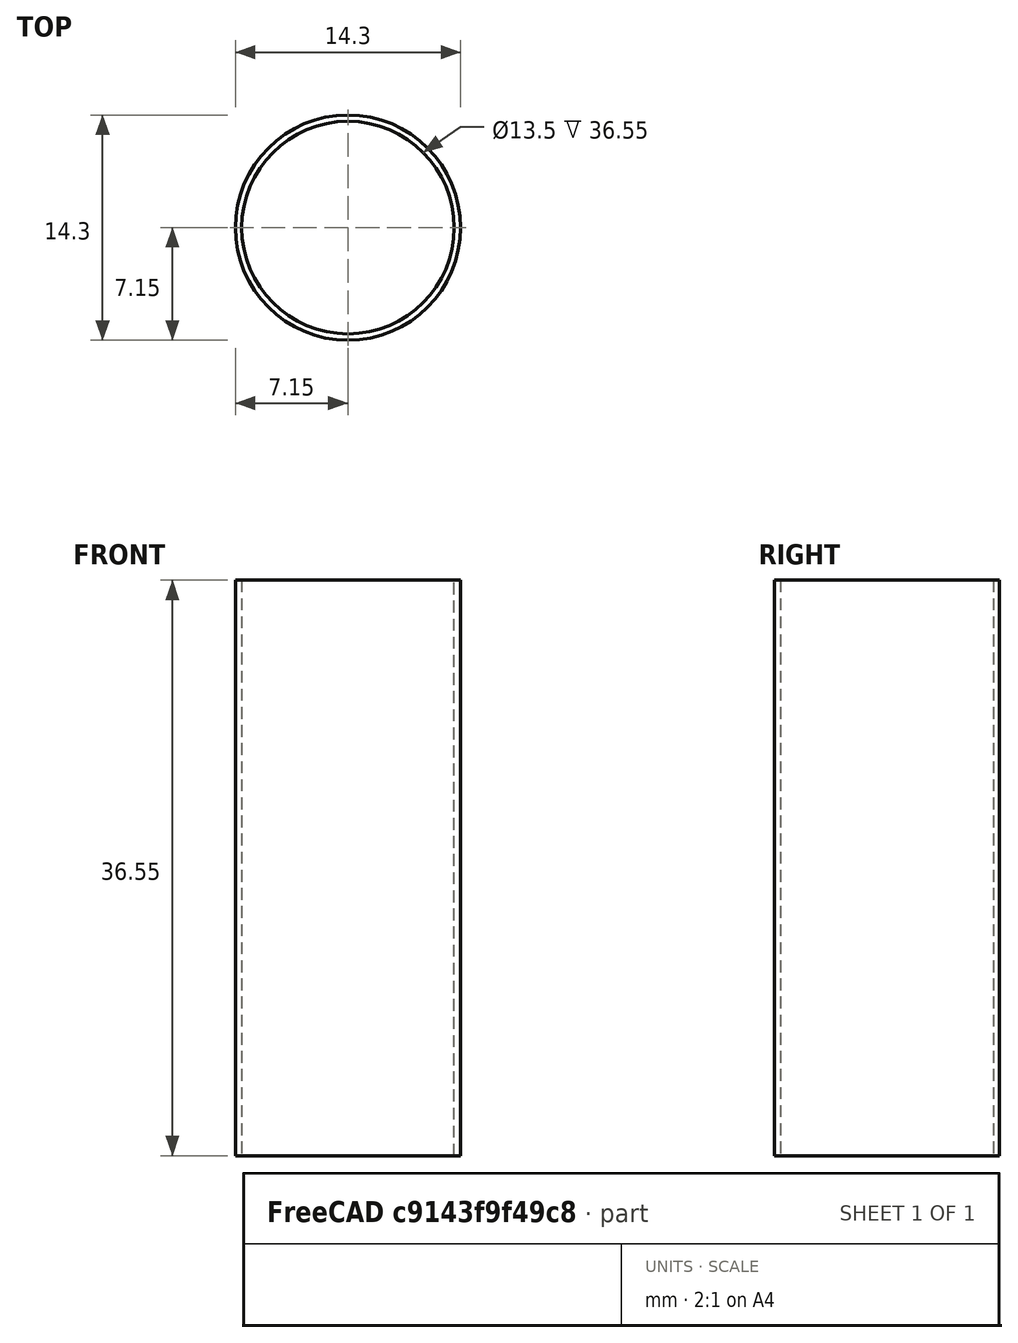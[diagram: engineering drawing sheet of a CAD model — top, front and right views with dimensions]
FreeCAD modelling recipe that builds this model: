
FCSTD DOCUMENT  (FreeCAD 0.20R27422 (Git))
Label: Tube
License: All rights reserved
LicenseURL: http://en.wikipedia.org/wiki/All_rights_reserved
objects: Sketcher::SketchObject×1, PartDesign::Pad×1, PartDesign::Body×1
note: 4 computed .brp shape members not serialized (recipe doc carries the construction recipe); baked Part::Feature solids carry a one-line shape summary decoded from their .brp

FEATURE [Sketcher::SketchObject] Sketch
  FullyConstrained = true
  MapMode = 5
  Support = -> [XY_Plane]
  sketch-geometry (2):
    g0: Circle CenterX=0 CenterY=0 CenterZ=0 NormalX=0 NormalY=0 NormalZ=1 AngleXU=0 Radius=6.75
    g1: Circle CenterX=0 CenterY=0 CenterZ=0 NormalX=0 NormalY=0 NormalZ=1 AngleXU=0 Radius=7.15
  constraints (4):
    c: Coincident(g0,g-1)
    c: Diameter(g0) = 13.5
    c: Coincident(g1,g0)
    c: Diameter(g1) = 14.3
FEATURE [PartDesign::Pad] Pad
  Direction = (0,0,1)
  Length = 36.55
  Length2 = 100
  Profile = -> Sketch
  ReferenceAxis = -> Sketch [N_Axis]
  Type = 0
FEATURE [PartDesign::Body] Body
  Group = -> [Sketch,Pad]
  Origin = -> Origin
  Tip = -> Pad
